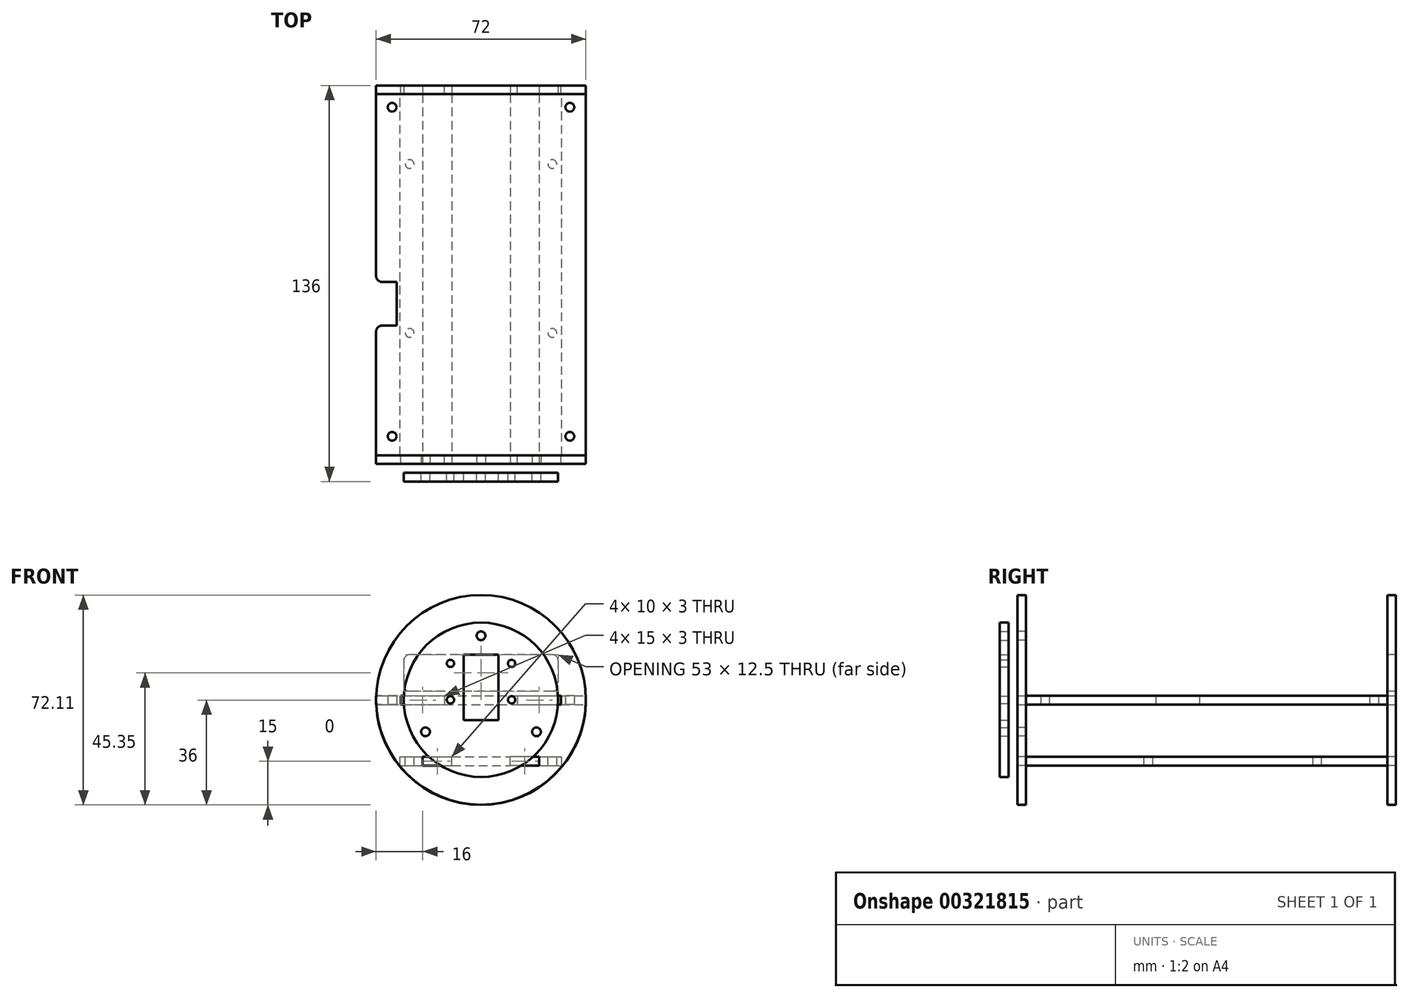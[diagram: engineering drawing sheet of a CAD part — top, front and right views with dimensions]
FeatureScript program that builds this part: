
annotation { "Feature Type Name" : "Feature", "Feature Type Description" : "" }
export const myFeature = defineFeature(function(context is Context, id is Id, definition is map)
    precondition{}
    {
        {
            var Q0;
            Q0=qCreatedBy(makeId("Top.planeOp"),FACE);
            var sketch = newSketch(context, id + "F0", { "sketchPlane" : qUnion([Q0])});
            skLineSegment(sketch, "E0.bottom", {"start": v(-34, 61) * mm, "end": v(34, 61) * mm, "construction": true});
            skLineSegment(sketch, "E0.top", {"start": v(-34, -59) * mm, "end": v(34, -59) * mm, "construction": true});
            skLineSegment(sketch, "E0.left", {"start": v(-34, 61) * mm, "end": v(-34, -59) * mm, "construction": true});
            skLineSegment(sketch, "E0.right", {"start": v(34, 61) * mm, "end": v(34, -59) * mm, "construction": true});
            skPoint(sketch, "E0.middle", {"position": v(0, 0) * mm});
            skCircle(sketch, "E1", {"center": v(-30.5, 57.5) * mm, "radius": 1.5 * mm});
            skCircle(sketch, "E2", {"center": v(30.5, 57.5) * mm, "radius": 1.5 * mm});
            skCircle(sketch, "E3", {"center": v(-30.5, -55.5) * mm, "radius": 1.5 * mm});
            skCircle(sketch, "E4", {"center": v(30.5, -55.5) * mm, "radius": 1.5 * mm});
            skLineSegment(sketch, "E5.bottom", {"start": v(-36, 62) * mm, "end": v(36, 62) * mm});
            skLineSegment(sketch, "E5.top", {"start": v(-36, -62) * mm, "end": v(36, -62) * mm});
            skLineSegment(sketch, "E5.left", {"start": v(-36, 62) * mm, "end": v(-36, -62) * mm});
            skLineSegment(sketch, "E5.right", {"start": v(36, 62) * mm, "end": v(36, -62) * mm});
            skLineSegment(sketch, "E6.bottom", {"start": v(-24, -3.98) * mm, "end": v(-34, -3.98) * mm, "construction": true});
            skLineSegment(sketch, "E6.top", {"start": v(-24, -15.98) * mm, "end": v(-34, -15.98) * mm, "construction": true});
            skLineSegment(sketch, "E6.left", {"start": v(-24, -3.98) * mm, "end": v(-24, -15.98) * mm, "construction": true});
            skLineSegment(sketch, "E6.right", {"start": v(-34, -3.98) * mm, "end": v(-34, -15.98) * mm, "construction": true});
            skPoint(sketch, "E6.middle", {"position": v(-29, -9.98) * mm});
            skLineSegment(sketch, "E7", {"start": v(-36, -2.48) * mm, "end": v(-29, -2.48) * mm});
            skPoint(sketch, "E7.endSnap0", {"position": v(-29, -3.98) * mm});
            skLineSegment(sketch, "E8", {"start": v(-29, -2.48) * mm, "end": v(-29, -17.48) * mm});
            skLineSegment(sketch, "E9", {"start": v(-29, -17.48) * mm, "end": v(-36, -17.48) * mm});
            skLineSegment(sketch, "E10.bottom", {"start": v(27.5, -62) * mm, "end": v(12.5, -62) * mm});
            skLineSegment(sketch, "E10.top", {"start": v(27.5, -65) * mm, "end": v(12.5, -65) * mm});
            skLineSegment(sketch, "E10.left", {"start": v(27.5, -62) * mm, "end": v(27.5, -65) * mm});
            skLineSegment(sketch, "E10.right", {"start": v(12.5, -62) * mm, "end": v(12.5, -65) * mm});
            skPoint(sketch, "E10.middle", {"position": v(20, -63.5) * mm});
            skLineSegment(sketch, "E11", {"start": v(22.63, 0) * mm, "end": v(0, 0) * mm, "construction": true});
            skLineSegment(sketch, "E12", {"start": v(0, 0) * mm, "end": v(0, -27.49) * mm, "construction": true});
            skLineSegment(sketch, "E13.MirrorCS", {"start": v(27.5, 62) * mm, "end": v(27.5, 65) * mm});
            skLineSegment(sketch, "E14.MirrorCS", {"start": v(27.5, 65) * mm, "end": v(12.5, 65) * mm});
            skLineSegment(sketch, "E15.MirrorCS", {"start": v(12.5, 62) * mm, "end": v(12.5, 65) * mm});
            skLineSegment(sketch, "E16.MirrorCS", {"start": v(-27.5, 62) * mm, "end": v(-27.5, 65) * mm});
            skLineSegment(sketch, "E17.MirrorCS", {"start": v(-27.5, 65) * mm, "end": v(-12.5, 65) * mm});
            skLineSegment(sketch, "E18.MirrorCS", {"start": v(-12.5, 62) * mm, "end": v(-12.5, 65) * mm});
            skLineSegment(sketch, "E19.MirrorCS", {"start": v(-27.5, -62) * mm, "end": v(-27.5, -65) * mm});
            skLineSegment(sketch, "E20.MirrorCS", {"start": v(-27.5, -65) * mm, "end": v(-12.5, -65) * mm});
            skLineSegment(sketch, "E21.MirrorCS", {"start": v(-12.5, -62) * mm, "end": v(-12.5, -65) * mm});
            skSolve(sketch);
        }
        {
            var Q0;
            Q0=makeQuery(id+"F0.imprint","IMPRINT",FACE,{"disambiguationData":[TD([[makeQuery(id+"F0.imprint","IMPRINT",EDGE,{"derivedFrom":sQuery(id+"F0.wireOp",EDGE,"E1")}),-1.0]])]});
            var Q1;
            {var subQ0=sQuery(id+"F0.wireOp",EDGE,"E13.MirrorCS");Q1=makeQuery(id+"F0.imprint","IMPRINT",FACE,{"disambiguationData":[TD([[makeQuery(id+"F0.imprint","IMPRINT",EDGE,{"derivedFrom":subQ0}),1.0]])]});}
            var Q2;
            {var subQ0=sQuery(id+"F0.wireOp",EDGE,"E16.MirrorCS");Q2=makeQuery(id+"F0.imprint","IMPRINT",FACE,{"disambiguationData":[TD([[makeQuery(id+"F0.imprint","IMPRINT",EDGE,{"derivedFrom":subQ0}),-1.0]])]});}
            var Q3;
            Q3=makeQuery(id+"F0.imprint","IMPRINT",FACE,{"disambiguationData":[TD([[makeQuery(id+"F0.imprint","IMPRINT",EDGE,{"derivedFrom":sQuery(id+"F0.wireOp",EDGE,"E10.bottom")}),1.0]])]});
            var Q4;
            {var subQ0=sQuery(id+"F0.wireOp",EDGE,"E19.MirrorCS");Q4=makeQuery(id+"F0.imprint","IMPRINT",FACE,{"disambiguationData":[TD([[makeQuery(id+"F0.imprint","IMPRINT",EDGE,{"derivedFrom":subQ0}),1.0]])]});}
            extrude(context, id + "F1", {"entities" : qUnion([Q0, Q1, Q2, Q3, Q4]), "depth" : 3 * mm});
        }
        {
            var Q0;
            Q0=makeQuery(id+"F1.opExtrude","SWEPT_EDGE",EDGE,{"disambiguationData":[OSD([sQuery(id+"F0.wireOp",EDGE,"E5.left"),sQuery(id+"F0.wireOp",EDGE,"E7")])]});
            var Q1;
            Q1=makeQuery(id+"F1.opExtrude","SWEPT_EDGE",EDGE,{"disambiguationData":[OSD([sQuery(id+"F0.wireOp",EDGE,"E5.left"),sQuery(id+"F0.wireOp",EDGE,"E9")])]});
            fillet(context, id + "F2", {"entities" : qUnion([Q0, Q1]), "radius" : 2 * mm, "tangentPropagation" : true, "allowEdgeOverflow" : false});
        }
        {
            var Q0;
            {var subQ0=sQuery(id+"F0.wireOp",EDGE,"E5.top");Q0=makeQuery(id+"F1.opExtrude","SWEPT_FACE",FACE,{"disambiguationData":[OSD([subQ0]),TDD([makeQuery(id+"F0.imprint","IMPRINT",EDGE,{"disambiguationData":[TD([[makeQuery(id+"F0.imprint","INTERSECT",VERTEX,{"derivedFrom":[subQ0,sQuery(id+"F0.wireOp",EDGE,"E21.MirrorCS")]}),-1.0]])],"derivedFrom":subQ0})])]});}
            var sketch = newSketch(context, id + "F3", { "sketchPlane" : qUnion([Q0])});
            skCircle(sketch, "E22", {"center": v(0, 1.61) * mm, "radius": 36 * mm});
            skLineSegment(sketch, "E23", {"start": v(0, 0) * mm, "end": v(0, 3) * mm, "construction": true});
            skLineSegment(sketch, "E24.0", {"start": v(-27.5, 3) * mm, "end": v(-12.5, 3) * mm});
            skLineSegment(sketch, "E24.1", {"start": v(-27.5, 3) * mm, "end": v(-27.5, 0) * mm});
            skLineSegment(sketch, "E24.2", {"start": v(-27.5, 0) * mm, "end": v(-12.5, 0) * mm});
            skLineSegment(sketch, "E24.3", {"start": v(-12.5, 3) * mm, "end": v(-12.5, 0) * mm});
            skLineSegment(sketch, "E24.4", {"start": v(27.5, 3) * mm, "end": v(12.5, 3) * mm});
            skLineSegment(sketch, "E24.5", {"start": v(12.5, 3) * mm, "end": v(12.5, 0) * mm});
            skLineSegment(sketch, "E24.6", {"start": v(27.5, 0) * mm, "end": v(12.5, 0) * mm});
            skLineSegment(sketch, "E24.7", {"start": v(27.5, 3) * mm, "end": v(27.5, 0) * mm});
            skSolve(sketch);
        }
        {
            var Q0;
            Q0 = qSketchRegion(id + "F3", true);
            extrude(context, id + "F4", {"entities" : qUnion([Q0]), "depth" : 3 * mm});
        }
        {
            var Q0;
            {var subQ0=sQuery(id+"F0.wireOp",EDGE,"E5.bottom");Q0=makeQuery(id+"F1.opExtrude","SWEPT_FACE",FACE,{"disambiguationData":[OSD([subQ0]),TDD([makeQuery(id+"F0.imprint","IMPRINT",EDGE,{"disambiguationData":[TD([[makeQuery(id+"F0.imprint","INTERSECT",VERTEX,{"derivedFrom":[subQ0,sQuery(id+"F0.wireOp",EDGE,"E15.MirrorCS")]}),1.0]])],"derivedFrom":subQ0})])]});}
            var sketch = newSketch(context, id + "F5", { "sketchPlane" : qUnion([Q0])});
            skLineSegment(sketch, "E25", {"start": v(0, 0) * mm, "end": v(0, 3) * mm, "construction": true});
            skPoint(sketch, "E26", {"position": v(0, 1.5) * mm});
            skCircle(sketch, "E27", {"center": v(0, 1.5) * mm, "radius": 36 * mm});
            skLineSegment(sketch, "E28.0", {"start": v(-27.5, 3) * mm, "end": v(-12.5, 3) * mm});
            skLineSegment(sketch, "E28.1", {"start": v(-27.5, 3) * mm, "end": v(-27.5, 0) * mm});
            skLineSegment(sketch, "E28.2", {"start": v(-27.5, 0) * mm, "end": v(-12.5, 0) * mm});
            skLineSegment(sketch, "E28.3", {"start": v(-12.5, 3) * mm, "end": v(-12.5, 0) * mm});
            skLineSegment(sketch, "E28.4", {"start": v(27.5, 3) * mm, "end": v(12.5, 3) * mm});
            skLineSegment(sketch, "E28.5", {"start": v(12.5, 3) * mm, "end": v(12.5, 0) * mm});
            skLineSegment(sketch, "E28.6", {"start": v(27.5, 0) * mm, "end": v(12.5, 0) * mm});
            skLineSegment(sketch, "E28.7", {"start": v(27.5, 3) * mm, "end": v(27.5, 0) * mm});
            skLineSegment(sketch, "E29.bottom", {"start": v(-24.5, 17.1) * mm, "end": v(24.5, 17.1) * mm});
            skLineSegment(sketch, "E29.top", {"start": v(-24.5, 4.6) * mm, "end": v(24.5, 4.6) * mm});
            skLineSegment(sketch, "E29.left", {"start": v(-26.5, 15.1) * mm, "end": v(-26.5, 6.6) * mm});
            skLineSegment(sketch, "E29.right", {"start": v(26.5, 15.1) * mm, "end": v(26.5, 6.6) * mm});
            skPoint(sketch, "E29.middle", {"position": v(0, 10.85) * mm});
            skPoint(sketch, "E30.visualSharp", {"position": v(-26.5, 17.1) * mm});
            skArc(sketch, "E30.filletArc", {"start": v(-24.5, 17.1) * mm, "mid": v(-25.91, 16.51) * mm, "end": v(-26.5, 15.1) * mm});
            skPoint(sketch, "E31.visualSharp", {"position": v(-26.5, 4.6) * mm});
            skArc(sketch, "E31.filletArc", {"start": v(-26.5, 6.6) * mm, "mid": v(-25.91, 5.19) * mm, "end": v(-24.5, 4.6) * mm});
            skPoint(sketch, "E32.visualSharp", {"position": v(26.5, 4.6) * mm});
            skArc(sketch, "E32.filletArc", {"start": v(24.5, 4.6) * mm, "mid": v(25.91, 5.19) * mm, "end": v(26.5, 6.6) * mm});
            skPoint(sketch, "E33.visualSharp", {"position": v(26.5, 17.1) * mm});
            skArc(sketch, "E33.filletArc", {"start": v(26.5, 15.1) * mm, "mid": v(25.91, 16.51) * mm, "end": v(24.5, 17.1) * mm});
            skSolve(sketch);
        }
        {
            var Q0;
            Q0 = qSketchRegion(id + "F5", true);
            extrude(context, id + "F6", {"entities" : qUnion([Q0]), "depth" : 3 * mm});
        }
        {
            var Q0;
            Q0=makeQuery(id+"F1.opExtrude","CAP_FACE",FACE,{"disambiguationData":[OSD([sQuery(id+"F0.wireOp",EDGE,"E1"),sQuery(id+"F0.wireOp",EDGE,"E2"),sQuery(id+"F0.wireOp",EDGE,"E3"),sQuery(id+"F0.wireOp",EDGE,"E4"),sQuery(id+"F0.wireOp",EDGE,"E5.bottom"),sQuery(id+"F0.wireOp",EDGE,"E5.top"),sQuery(id+"F0.wireOp",EDGE,"E5.left"),sQuery(id+"F0.wireOp",EDGE,"E5.right"),sQuery(id+"F0.wireOp",EDGE,"E7"),sQuery(id+"F0.wireOp",EDGE,"E8"),sQuery(id+"F0.wireOp",EDGE,"E9"),sQuery(id+"F0.wireOp",EDGE,"E10.top"),sQuery(id+"F0.wireOp",EDGE,"E10.left"),sQuery(id+"F0.wireOp",EDGE,"E10.right"),sQuery(id+"F0.wireOp",EDGE,"E13.MirrorCS"),sQuery(id+"F0.wireOp",EDGE,"E14.MirrorCS"),sQuery(id+"F0.wireOp",EDGE,"E15.MirrorCS"),sQuery(id+"F0.wireOp",EDGE,"E16.MirrorCS"),sQuery(id+"F0.wireOp",EDGE,"E17.MirrorCS"),sQuery(id+"F0.wireOp",EDGE,"E18.MirrorCS"),sQuery(id+"F0.wireOp",EDGE,"E19.MirrorCS"),sQuery(id+"F0.wireOp",EDGE,"E20.MirrorCS"),sQuery(id+"F0.wireOp",EDGE,"E21.MirrorCS")])],"isStart":true});
            cPlane(context, id + "F7", {"entities" : qUnion([Q0]), "cplaneType" : CPlaneType.OFFSET, "offset" : 18 * mm, "width" : 150 * mm, "height" : 150 * mm});
        }
        {
            var Q0;
            Q0=qCreatedBy(id+"F7.planeOp",FACE);
            var sketch = newSketch(context, id + "F8", { "sketchPlane" : qUnion([Q0])});
            skLineSegment(sketch, "E34.bottom", {"start": v(-27.75, 62) * mm, "end": v(27.75, 62) * mm});
            skLineSegment(sketch, "E34.top", {"start": v(-27.75, -62) * mm, "end": v(27.75, -62) * mm});
            skLineSegment(sketch, "E34.left", {"start": v(-27.75, 62) * mm, "end": v(-27.75, -62) * mm});
            skLineSegment(sketch, "E34.right", {"start": v(27.75, 62) * mm, "end": v(27.75, -62) * mm});
            skPoint(sketch, "E34.middle", {"position": v(0, 0) * mm});
            skLineSegment(sketch, "E35.bottom", {"start": v(-20, 62) * mm, "end": v(-10, 62) * mm});
            skLineSegment(sketch, "E35.top", {"start": v(-20, 65) * mm, "end": v(-10, 65) * mm});
            skLineSegment(sketch, "E35.left", {"start": v(-20, 62) * mm, "end": v(-20, 65) * mm});
            skLineSegment(sketch, "E35.right", {"start": v(-10, 62) * mm, "end": v(-10, 65) * mm});
            skPoint(sketch, "E35.middle", {"position": v(-15, 63.5) * mm});
            skLineSegment(sketch, "E36", {"start": v(0, 27.21) * mm, "end": v(0, 0) * mm, "construction": true});
            skLineSegment(sketch, "E37", {"start": v(0, 0) * mm, "end": v(20.44, 0) * mm, "construction": true});
            skLineSegment(sketch, "E38.MirrorCS", {"start": v(10, 62) * mm, "end": v(10, 65) * mm});
            skLineSegment(sketch, "E39.MirrorCS", {"start": v(20, 65) * mm, "end": v(10, 65) * mm});
            skLineSegment(sketch, "E40.MirrorCS", {"start": v(20, 62) * mm, "end": v(20, 65) * mm});
            skLineSegment(sketch, "E41.MirrorCS", {"start": v(20, -62) * mm, "end": v(20, -65) * mm});
            skLineSegment(sketch, "E42.MirrorCS", {"start": v(20, -65) * mm, "end": v(10, -65) * mm});
            skLineSegment(sketch, "E43.MirrorCS", {"start": v(10, -62) * mm, "end": v(10, -65) * mm});
            skLineSegment(sketch, "E44.MirrorCS", {"start": v(-10, -62) * mm, "end": v(-10, -65) * mm});
            skLineSegment(sketch, "E45.MirrorCS", {"start": v(-20, -65) * mm, "end": v(-10, -65) * mm});
            skLineSegment(sketch, "E46.MirrorCS", {"start": v(-20, -62) * mm, "end": v(-20, -65) * mm});
            skCircle(sketch, "E47", {"center": v(24.5, 20) * mm, "radius": 1.5 * mm});
            skCircle(sketch, "E48", {"center": v(24.5, -38) * mm, "radius": 1.5 * mm});
            skCircle(sketch, "E49", {"center": v(-24.5, -38) * mm, "radius": 1.5 * mm});
            skCircle(sketch, "E50", {"center": v(-24.5, 20) * mm, "radius": 1.5 * mm});
            skLineSegment(sketch, "E51", {"start": v(24.5, 20) * mm, "end": v(-24.5, 20) * mm, "construction": true});
            skPoint(sketch, "E52", {"position": v(0, 20) * mm});
            skSolve(sketch);
        }
        {
            var Q0;
            Q0 = qSketchRegion(id + "F8", true);
            extrude(context, id + "F9", {"entities" : qUnion([Q0]), "depth" : 3 * mm});
        }
        {
            var Q0;
            Q0=makeQuery(id+"F4.opExtrude","CAP_FACE",FACE,{"disambiguationData":[OSD([sQuery(id+"F3.wireOp",EDGE,"E22"),sQuery(id+"F3.wireOp",EDGE,"E24.0"),sQuery(id+"F3.wireOp",EDGE,"E24.1"),sQuery(id+"F3.wireOp",EDGE,"E24.2"),sQuery(id+"F3.wireOp",EDGE,"E24.3"),sQuery(id+"F3.wireOp",EDGE,"E24.4"),sQuery(id+"F3.wireOp",EDGE,"E24.5"),sQuery(id+"F3.wireOp",EDGE,"E24.6"),sQuery(id+"F3.wireOp",EDGE,"E24.7")])],"isStart":false});
            var sketch = newSketch(context, id + "F10", { "sketchPlane" : qUnion([Q0])});
            skLineSegment(sketch, "E53.0", {"start": v(-20, -18) * mm, "end": v(-10, -18) * mm});
            skLineSegment(sketch, "E53.1", {"start": v(-20, -21) * mm, "end": v(-20, -18) * mm});
            skLineSegment(sketch, "E53.2", {"start": v(-20, -21) * mm, "end": v(-10, -21) * mm});
            skLineSegment(sketch, "E53.3", {"start": v(-10, -21) * mm, "end": v(-10, -18) * mm});
            skLineSegment(sketch, "E53.4", {"start": v(20, -18) * mm, "end": v(10, -18) * mm});
            skLineSegment(sketch, "E53.5", {"start": v(10, -21) * mm, "end": v(10, -18) * mm});
            skLineSegment(sketch, "E53.6", {"start": v(20, -21) * mm, "end": v(10, -21) * mm});
            skLineSegment(sketch, "E53.7", {"start": v(20, -21) * mm, "end": v(20, -18) * mm});
            skSolve(sketch);
        }
        {
            var Q0;
            Q0 = qSketchRegion(id + "F10", true);
            var Q1;
            Q1=makeQuery(id+"F6.opExtrude","CAP_FACE",FACE,{"disambiguationData":[OSD([sQuery(id+"F5.wireOp",EDGE,"E27"),sQuery(id+"F5.wireOp",EDGE,"E28.0"),sQuery(id+"F5.wireOp",EDGE,"E28.1"),sQuery(id+"F5.wireOp",EDGE,"E28.2"),sQuery(id+"F5.wireOp",EDGE,"E28.3"),sQuery(id+"F5.wireOp",EDGE,"E28.4"),sQuery(id+"F5.wireOp",EDGE,"E28.5"),sQuery(id+"F5.wireOp",EDGE,"E28.6"),sQuery(id+"F5.wireOp",EDGE,"E28.7"),sQuery(id+"F5.wireOp",EDGE,"E29.bottom"),sQuery(id+"F5.wireOp",EDGE,"E29.top"),sQuery(id+"F5.wireOp",EDGE,"E29.left"),sQuery(id+"F5.wireOp",EDGE,"E29.right"),sQuery(id+"F5.wireOp",EDGE,"E30.filletArc"),sQuery(id+"F5.wireOp",EDGE,"E31.filletArc"),sQuery(id+"F5.wireOp",EDGE,"E32.filletArc"),sQuery(id+"F5.wireOp",EDGE,"E33.filletArc")])],"isStart":false});
            extrude(context, id + "F11", {"entities" : qUnion([Q0]), "operationType" : NewBodyOperationType.REMOVE, "endBound" : BoundingType.UP_TO_SURFACE, "oppositeDirection" : true, "endBoundEntityFace" : qUnion([Q1]), "depth" : 25 * mm});
        }
        {
            var Q0;
            Q0=makeQuery(id+"F4.opExtrude","CAP_FACE",FACE,{"disambiguationData":[OSD([sQuery(id+"F3.wireOp",EDGE,"E22"),sQuery(id+"F3.wireOp",EDGE,"E24.0"),sQuery(id+"F3.wireOp",EDGE,"E24.1"),sQuery(id+"F3.wireOp",EDGE,"E24.2"),sQuery(id+"F3.wireOp",EDGE,"E24.3"),sQuery(id+"F3.wireOp",EDGE,"E24.4"),sQuery(id+"F3.wireOp",EDGE,"E24.5"),sQuery(id+"F3.wireOp",EDGE,"E24.6"),sQuery(id+"F3.wireOp",EDGE,"E24.7")])],"isStart":false});
            cPlane(context, id + "F12", {"entities" : qUnion([Q0]), "cplaneType" : CPlaneType.OFFSET, "offset" : 3 * mm, "width" : 150 * mm, "height" : 150 * mm});
        }
        {
            var Q0;
            Q0=qCreatedBy(id+"F12.planeOp",FACE);
            var sketch = newSketch(context, id + "F13", { "sketchPlane" : qUnion([Q0])});
            skCircle(sketch, "E54.0", {"center": v(0, 1.61) * mm, "radius": 36 * mm, "construction": true});
            skLineSegment(sketch, "E55.bottom", {"start": v(-4, 5.61) * mm, "end": v(4, 5.61) * mm, "construction": true});
            skLineSegment(sketch, "E55.top", {"start": v(-4, -2.39) * mm, "end": v(4, -2.39) * mm, "construction": true});
            skLineSegment(sketch, "E55.left", {"start": v(-4, 5.61) * mm, "end": v(-4, -2.39) * mm, "construction": true});
            skLineSegment(sketch, "E55.right", {"start": v(4, 5.61) * mm, "end": v(4, -2.39) * mm, "construction": true});
            skCircle(sketch, "E56", {"center": v(-10.5, 1.61) * mm, "radius": 1.25 * mm});
            skCircle(sketch, "E57", {"center": v(10.5, 1.61) * mm, "radius": 1.25 * mm});
            skCircle(sketch, "E58", {"center": v(10.5, 14.11) * mm, "radius": 1.25 * mm});
            skCircle(sketch, "E59", {"center": v(-10.5, 14.11) * mm, "radius": 1.25 * mm});
            skLineSegment(sketch, "E60", {"start": v(-10.5, 1.61) * mm, "end": v(10.5, 1.61) * mm, "construction": true});
            skLineSegment(sketch, "E61.bottom", {"start": v(-6, 17.11) * mm, "end": v(6, 17.11) * mm});
            skLineSegment(sketch, "E61.top", {"start": v(-6, -5.39) * mm, "end": v(6, -5.39) * mm});
            skLineSegment(sketch, "E61.left", {"start": v(-6, 17.11) * mm, "end": v(-6, -5.39) * mm});
            skLineSegment(sketch, "E61.right", {"start": v(6, 17.11) * mm, "end": v(6, -5.39) * mm});
            skPoint(sketch, "E61.middle", {"position": v(0, 5.86) * mm});
            skCircle(sketch, "E62", {"center": v(0, 1.61) * mm, "radius": 26.5 * mm});
            skCircle(sketch, "E63", {"center": v(0, 23.61) * mm, "radius": 1.5 * mm});
            skCircle(sketch, "E64.1.0", {"center": v(-19.05, -9.39) * mm, "radius": 1.5 * mm});
            skCircle(sketch, "E64.2.0", {"center": v(19.05, -9.39) * mm, "radius": 1.5 * mm});
            skSolve(sketch);
        }
        {
            var Q0;
            Q0 = qSketchRegion(id + "F13", true);
            extrude(context, id + "F14", {"entities" : qUnion([Q0]), "depth" : 3 * mm});
        }
        {
            var Q0;
            Q0=makeQuery(id+"F13.imprint","IMPRINT",FACE,{"disambiguationData":[TD([[makeQuery(id+"F13.imprint","IMPRINT",EDGE,{"derivedFrom":sQuery(id+"F13.wireOp",EDGE,"E63")}),1.0]])]});
            var Q1;
            Q1=makeQuery(id+"F13.imprint","IMPRINT",FACE,{"disambiguationData":[TD([[makeQuery(id+"F13.imprint","IMPRINT",EDGE,{"derivedFrom":sQuery(id+"F13.wireOp",EDGE,"E64.1.0")}),1.0]])]});
            var Q2;
            Q2=makeQuery(id+"F13.imprint","IMPRINT",FACE,{"disambiguationData":[TD([[makeQuery(id+"F13.imprint","IMPRINT",EDGE,{"derivedFrom":sQuery(id+"F13.wireOp",EDGE,"E64.2.0")}),1.0]])]});
            extrude(context, id + "F15", {"entities" : qUnion([Q0, Q1, Q2]), "operationType" : NewBodyOperationType.REMOVE, "oppositeDirection" : true, "depth" : 25 * mm});
        }
    });
